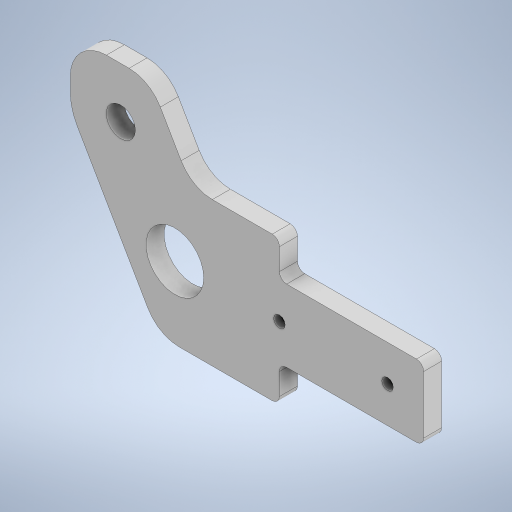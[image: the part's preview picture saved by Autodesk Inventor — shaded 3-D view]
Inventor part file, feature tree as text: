
AUTODESK INVENTOR PART (.ipt)
format: ipt  version: 2024.3 (Build 283343000, 343)  size: 323,072 bytes
history: native  units: mm
features: sketch x4, extrude x3, fillet x2, other x1, hole x1, mirror x1
ambient origin geometry x8: Origin, YZ Plane, XZ Plane, XY Plane, X Axis, Y Axis, Z Axis, Center Point
bodies: Body1 (feature_tree)
feature tree (12):
  other  "ソリッド1"
  extrude  "押し出し1"  Depth=98.0mm
  hole  "穴1"  [1 undecoded]
  fillet  "フィレット1"  Radius=40.0mm
  fillet  "フィレット2"  Radius=20.0mm
  extrude  "押し出し2"  Depth=10.0mm
  mirror  "ミラー1"
  extrude  "押し出し3"  Depth=69.0mm
  sketch  "スケッチ1"
  sketch  "スケッチ2"
  sketch  "スケッチ4"
  sketch  "スケッチ5"
note: 1 required parameter value undecoded (feature->parameter linkage not recoverable at this tier; creation-order binding heuristic only, values carry confidence <= 0.55)
